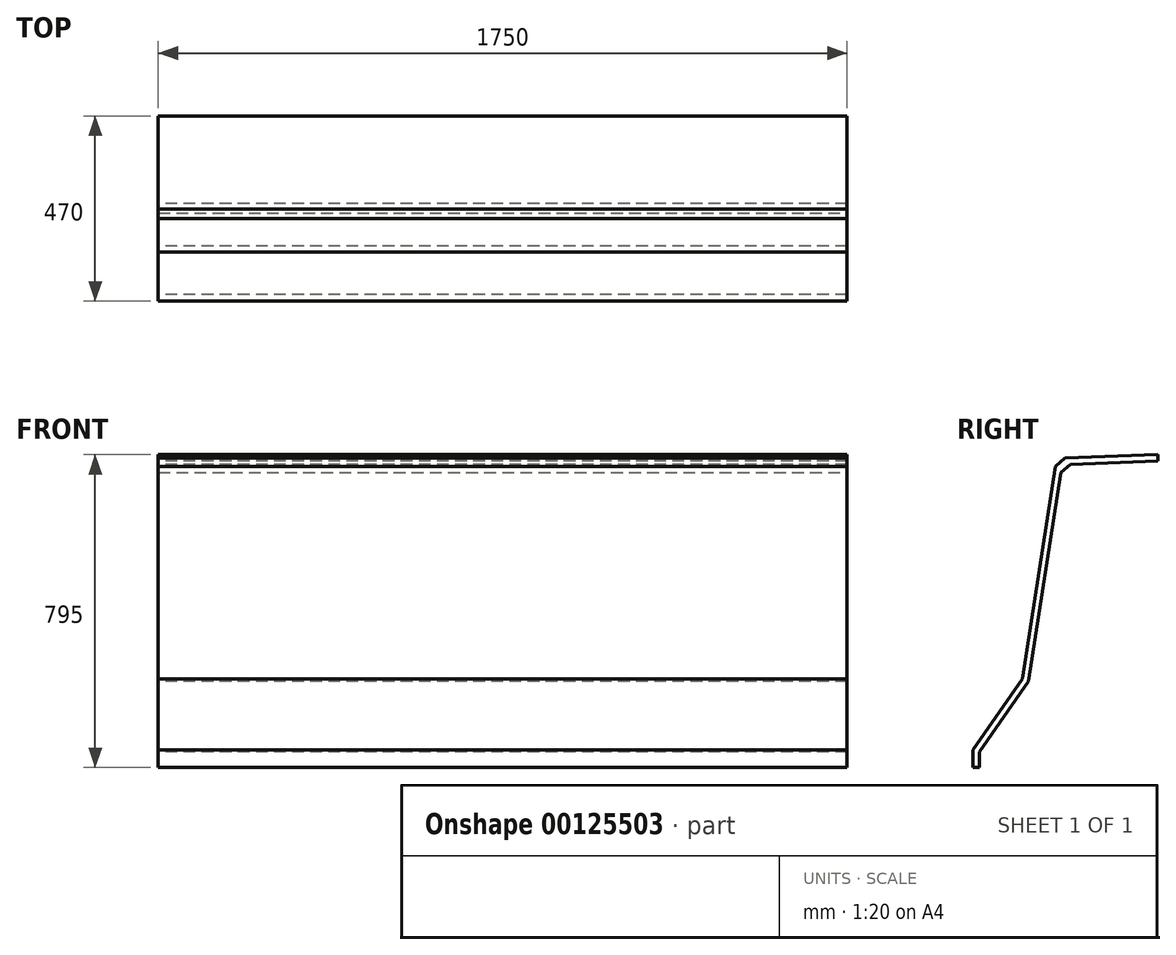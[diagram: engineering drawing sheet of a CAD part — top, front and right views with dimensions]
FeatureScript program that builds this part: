
annotation { "Feature Type Name" : "Feature", "Feature Type Description" : "" }
export const myFeature = defineFeature(function(context is Context, id is Id, definition is map)
    precondition{}
    {
        {
            var Q0;
            Q0=qCreatedBy(makeId("Right.planeOp"),FACE);
            var sketch = newSketch(context, id + "F0", { "sketchPlane" : qUnion([Q0])});
            skLineSegment(sketch, "E0", {"start": v(-53.43, -224.79) * mm, "end": v(-53.43, -179.79) * mm});
            skLineSegment(sketch, "E1", {"start": v(-53.43, -179.79) * mm, "end": v(71.57, 0.21) * mm});
            skLineSegment(sketch, "E2", {"start": v(71.57, 0.21) * mm, "end": v(159.57, 560.21) * mm});
            skLineSegment(sketch, "E3", {"start": v(159.57, 560.21) * mm, "end": v(416.57, 570.21) * mm});
            skLineSegment(sketch, "E4.0", {"start": v(173.33, 544.74) * mm, "end": v(416.57, 554.2) * mm});
            skLineSegment(sketch, "E4.1", {"start": v(86.8, -5.9) * mm, "end": v(173.33, 544.74) * mm});
            skLineSegment(sketch, "E4.2", {"start": v(-37.43, -184.8) * mm, "end": v(86.8, -5.9) * mm});
            skLineSegment(sketch, "E4.3", {"start": v(-37.43, -224.79) * mm, "end": v(-37.43, -184.8) * mm});
            skLineSegment(sketch, "E5", {"start": v(416.57, 570.21) * mm, "end": v(416.57, 554.2) * mm});
            skLineSegment(sketch, "E6", {"start": v(-53.43, -224.79) * mm, "end": v(-37.43, -224.79) * mm});
            skSolve(sketch);
        }
        {
            var Q0;
            Q0=makeQuery(id+"F0.imprint","IMPRINT",FACE,{"disambiguationData":[TD([[makeQuery(id+"F0.imprint","IMPRINT",EDGE,{"derivedFrom":sQuery(id+"F0.wireOp",EDGE,"E0")}),-1.0]])]});
            extrude(context, id + "F1", {"entities" : qUnion([Q0]), "endBound" : BoundingType.SYMMETRIC, "depth" : 1750 * mm});
        }
        {
            var Q0;
            Q0=makeQuery(id+"F1.opExtrude","SWEPT_EDGE",EDGE,{"disambiguationData":[OSD([sQuery(id+"F0.wireOp",EDGE,"E2"),sQuery(id+"F0.wireOp",EDGE,"E3")])]});
            var Q1;
            Q1=makeQuery(id+"F1.opExtrude","SWEPT_EDGE",EDGE,{"disambiguationData":[OSD([sQuery(id+"F0.wireOp",EDGE,"E4.0"),sQuery(id+"F0.wireOp",EDGE,"E4.1")])]});
            chamfer(context, id + "F2", {"entities" : qUnion([Q0, Q1]), "width" : 25 * mm, "tangentPropagation" : true});
        }
    });
